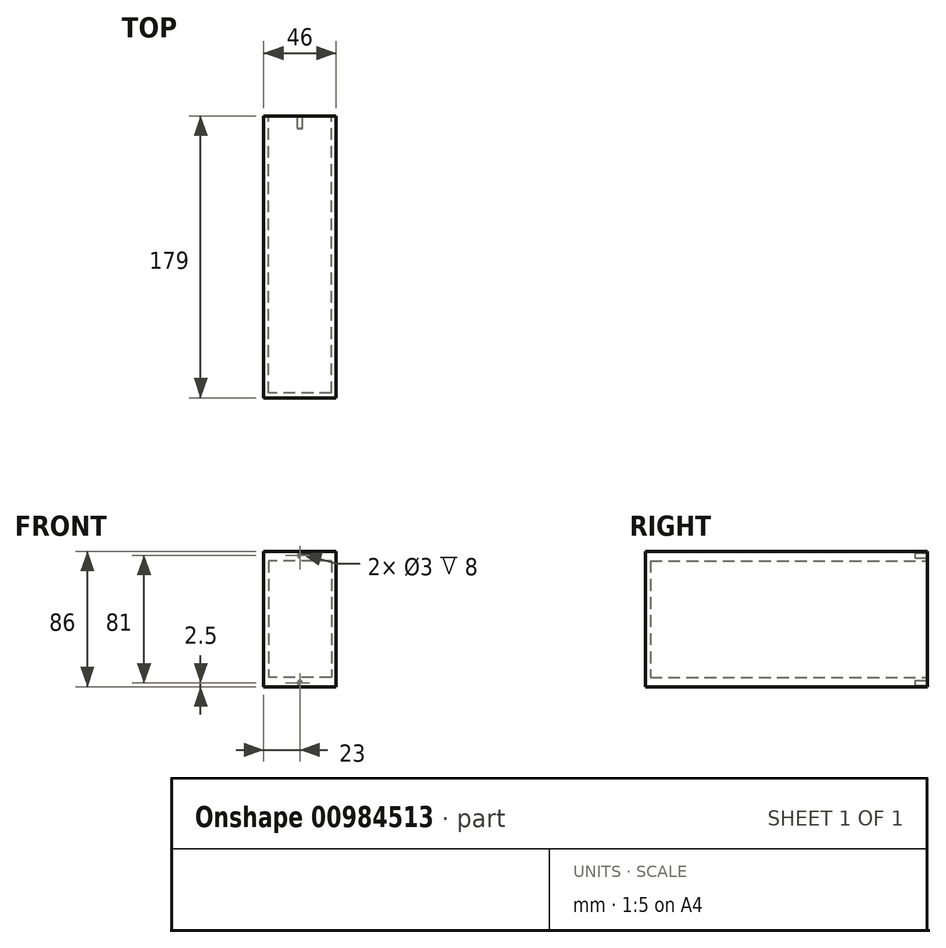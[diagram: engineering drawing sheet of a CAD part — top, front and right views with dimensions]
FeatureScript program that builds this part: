
annotation { "Feature Type Name" : "Feature", "Feature Type Description" : "" }
export const myFeature = defineFeature(function(context is Context, id is Id, definition is map)
    precondition{}
    {
        {
            var Q0;
            Q0=qCreatedBy(makeId("Front.planeOp"),FACE);
            var sketch = newSketch(context, id + "F0", { "sketchPlane" : qUnion([Q0])});
            skLineSegment(sketch, "E0.bottom", {"start": v(-23, 43) * mm, "end": v(23, 43) * mm});
            skLineSegment(sketch, "E0.top", {"start": v(-23, -43) * mm, "end": v(23, -43) * mm});
            skLineSegment(sketch, "E0.left", {"start": v(-23, 43) * mm, "end": v(-23, -43) * mm});
            skLineSegment(sketch, "E0.right", {"start": v(23, 43) * mm, "end": v(23, -43) * mm});
            skSolve(sketch);
        }
        {
            var Q0;
            Q0 = qSketchRegion(id + "F0", true);
            extrude(context, id + "F1", {"entities" : qUnion([Q0]), "depth" : 179 * mm, "offsetDistance" : 25 * mm});
        }
        {
            var Q0;
            Q0=makeQuery(id+"F1.opExtrude","CAP_FACE",FACE,{"disambiguationData":[OSD([sQuery(id+"F0.wireOp",EDGE,"E0.bottom"),sQuery(id+"F0.wireOp",EDGE,"E0.top"),sQuery(id+"F0.wireOp",EDGE,"E0.left"),sQuery(id+"F0.wireOp",EDGE,"E0.right")])],"isStart":true});
            var sketch = newSketch(context, id + "F2", { "sketchPlane" : qUnion([Q0])});
            skLineSegment(sketch, "E1.bottom", {"start": v(-20, 37) * mm, "end": v(20, 37) * mm});
            skLineSegment(sketch, "E1.top", {"start": v(-20, -37) * mm, "end": v(20, -37) * mm});
            skLineSegment(sketch, "E1.left", {"start": v(-20, 37) * mm, "end": v(-20, -37) * mm});
            skLineSegment(sketch, "E1.right", {"start": v(20, 37) * mm, "end": v(20, -37) * mm});
            skSolve(sketch);
        }
        {
            var Q0;
            Q0 = qSketchRegion(id + "F2", true);
            extrude(context, id + "F3", {"entities" : qUnion([Q0]), "operationType" : NewBodyOperationType.REMOVE, "oppositeDirection" : true, "depth" : 176 * mm, "offsetDistance" : 25 * mm});
        }
        {
            var Q0;
            Q0=makeQuery(id+"F1.opExtrude","CAP_FACE",FACE,{"disambiguationData":[OSD([sQuery(id+"F0.wireOp",EDGE,"E0.bottom"),sQuery(id+"F0.wireOp",EDGE,"E0.top"),sQuery(id+"F0.wireOp",EDGE,"E0.left"),sQuery(id+"F0.wireOp",EDGE,"E0.right")])],"isStart":true});
            var sketch = newSketch(context, id + "F4", { "sketchPlane" : qUnion([Q0])});
            skCircle(sketch, "E2", {"center": v(0, 40.5) * mm, "radius": 1.5 * mm});
            skCircle(sketch, "E3.MirrorC", {"center": v(0, -40.5) * mm, "radius": 1.5 * mm});
            skSolve(sketch);
        }
        {
            var Q0;
            Q0 = qSketchRegion(id + "F4", true);
            extrude(context, id + "F5", {"entities" : qUnion([Q0]), "operationType" : NewBodyOperationType.REMOVE, "oppositeDirection" : true, "depth" : 8 * mm, "offsetDistance" : 25 * mm});
        }
    });
